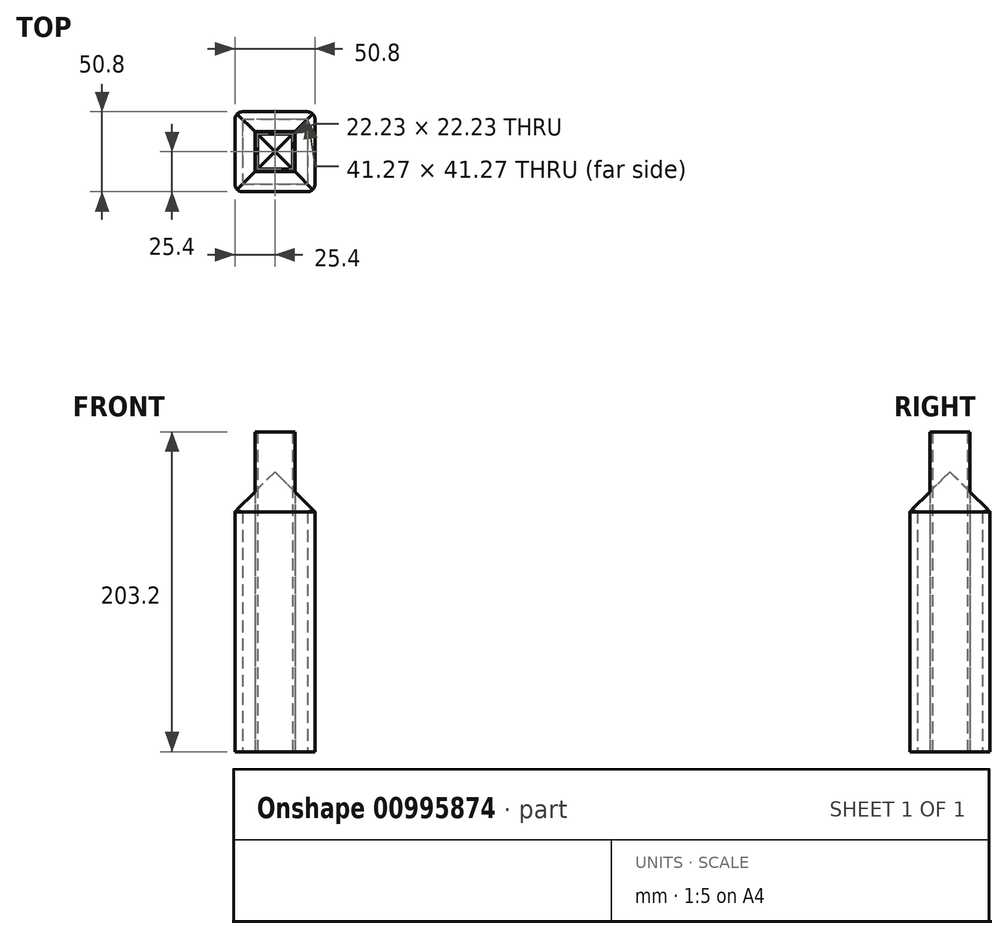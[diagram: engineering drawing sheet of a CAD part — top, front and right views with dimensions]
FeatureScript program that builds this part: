
annotation { "Feature Type Name" : "Feature", "Feature Type Description" : "" }
export const myFeature = defineFeature(function(context is Context, id is Id, definition is map)
    precondition{}
    {
        {
            var Q0;
            Q0=qCreatedBy(makeId("Top.planeOp"),FACE);
            var sketch = newSketch(context, id + "F0", { "sketchPlane" : qUnion([Q0])});
            skLineSegment(sketch, "E0.bottom", {"start": v(4.76, 0) * mm, "end": v(46.04, 0) * mm});
            skLineSegment(sketch, "E0.top", {"start": v(4.76, 50.8) * mm, "end": v(46.04, 50.8) * mm});
            skLineSegment(sketch, "E0.left", {"start": v(0, 4.76) * mm, "end": v(0, 46.04) * mm});
            skLineSegment(sketch, "E0.right", {"start": v(50.8, 4.76) * mm, "end": v(50.8, 46.04) * mm});
            skLineSegment(sketch, "E1.bottom", {"start": v(4.76, 46.04) * mm, "end": v(46.04, 46.04) * mm});
            skLineSegment(sketch, "E1.top", {"start": v(4.76, 4.76) * mm, "end": v(46.04, 4.76) * mm});
            skLineSegment(sketch, "E1.left", {"start": v(4.76, 46.04) * mm, "end": v(4.76, 4.76) * mm});
            skLineSegment(sketch, "E1.right", {"start": v(46.04, 46.04) * mm, "end": v(46.04, 4.76) * mm});
            skPoint(sketch, "E2.visualSharp", {"position": v(0, 50.8) * mm});
            skArc(sketch, "E2.filletArc", {"start": v(4.76, 50.8) * mm, "mid": v(1.4, 49.4) * mm, "end": v(0, 46.04) * mm});
            skPoint(sketch, "E3.visualSharp", {"position": v(50.8, 50.8) * mm});
            skArc(sketch, "E3.filletArc", {"start": v(50.8, 46.04) * mm, "mid": v(49.4, 49.4) * mm, "end": v(46.04, 50.8) * mm});
            skPoint(sketch, "E4.visualSharp", {"position": v(50.8, 0) * mm});
            skArc(sketch, "E4.filletArc", {"start": v(46.04, 0) * mm, "mid": v(49.4, 1.4) * mm, "end": v(50.8, 4.76) * mm});
            skPoint(sketch, "E5.visualSharp", {"position": v(0, 0) * mm});
            skArc(sketch, "E5.filletArc", {"start": v(0, 4.76) * mm, "mid": v(1.4, 1.4) * mm, "end": v(4.76, 0) * mm});
            skSolve(sketch);
        }
        {
            var Q0;
            Q0=makeQuery(id+"F0.imprint","IMPRINT",FACE,{"disambiguationData":[TD([[makeQuery(id+"F0.imprint","IMPRINT",EDGE,{"derivedFrom":sQuery(id+"F0.wireOp",EDGE,"E0.bottom")}),1.0]])]});
            extrude(context, id + "F1", {"entities" : qUnion([Q0]), "depth" : 152.4 * mm, "offsetDistance" : 25.4 * mm});
        }
        {
            var Q0;
            Q0=qCreatedBy(makeId("Top.planeOp"),FACE);
            var sketch = newSketch(context, id + "F2", { "sketchPlane" : qUnion([Q0])});
            skLineSegment(sketch, "E6.bottom", {"start": v(12.7, 38.1) * mm, "end": v(38.1, 38.1) * mm});
            skLineSegment(sketch, "E6.top", {"start": v(12.7, 12.7) * mm, "end": v(38.1, 12.7) * mm});
            skLineSegment(sketch, "E6.left", {"start": v(12.7, 38.1) * mm, "end": v(12.7, 12.7) * mm});
            skLineSegment(sketch, "E6.right", {"start": v(38.1, 38.1) * mm, "end": v(38.1, 12.7) * mm});
            skLineSegment(sketch, "E7.bottom", {"start": v(14.29, 36.51) * mm, "end": v(36.51, 36.51) * mm});
            skLineSegment(sketch, "E7.top", {"start": v(14.29, 14.29) * mm, "end": v(36.51, 14.29) * mm});
            skLineSegment(sketch, "E7.left", {"start": v(14.29, 36.51) * mm, "end": v(14.29, 14.29) * mm});
            skLineSegment(sketch, "E7.right", {"start": v(36.51, 36.51) * mm, "end": v(36.51, 14.29) * mm});
            skSolve(sketch);
        }
        {
            var Q0;
            Q0=makeQuery(id+"F1.opExtrude","CAP_FACE",FACE,{"disambiguationData":[OSD([sQuery(id+"F0.wireOp",EDGE,"E0.bottom"),sQuery(id+"F0.wireOp",EDGE,"E0.top"),sQuery(id+"F0.wireOp",EDGE,"E0.left"),sQuery(id+"F0.wireOp",EDGE,"E0.right"),sQuery(id+"F0.wireOp",EDGE,"E1.bottom"),sQuery(id+"F0.wireOp",EDGE,"E1.top"),sQuery(id+"F0.wireOp",EDGE,"E1.left"),sQuery(id+"F0.wireOp",EDGE,"E1.right"),sQuery(id+"F0.wireOp",EDGE,"E2.filletArc"),sQuery(id+"F0.wireOp",EDGE,"E3.filletArc"),sQuery(id+"F0.wireOp",EDGE,"E4.filletArc"),sQuery(id+"F0.wireOp",EDGE,"E5.filletArc")])],"isStart":false});
            var sketch = newSketch(context, id + "F3", { "sketchPlane" : qUnion([Q0])});
            skPoint(sketch, "E8.oppositeSnap0", {"position": v(50.8, 25.4) * mm});
            skLineSegment(sketch, "E8.bottom", {"start": v(0, 0) * mm, "end": v(50.8, 0) * mm});
            skLineSegment(sketch, "E8.top", {"start": v(0, 50.8) * mm, "end": v(50.8, 50.8) * mm});
            skLineSegment(sketch, "E8.left", {"start": v(0, 0) * mm, "end": v(0, 50.8) * mm});
            skLineSegment(sketch, "E8.right", {"start": v(50.8, 0) * mm, "end": v(50.8, 50.8) * mm});
            skSolve(sketch);
        }
        {
            var Q0;
            Q0=makeQuery(id+"F3.imprint","IMPRINT",FACE,{"disambiguationData":[TD([[makeQuery(id+"F3.imprint","IMPRINT",EDGE,{"derivedFrom":makeQuery(id+"F1.opExtrude","CAP_EDGE",EDGE,{"disambiguationData":[OSD([sQuery(id+"F0.wireOp",EDGE,"E1.bottom")])],"isStart":false})}),-1.0]])]});
            var Q1;
            Q1=makeQuery(id+"F3.imprint","IMPRINT",FACE,{"disambiguationData":[TD([[makeQuery(id+"F3.imprint","IMPRINT",EDGE,{"derivedFrom":makeQuery(id+"F1.opExtrude","CAP_EDGE",EDGE,{"disambiguationData":[OSD([sQuery(id+"F0.wireOp",EDGE,"E1.bottom")])],"isStart":false})}),1.0]])]});
            extrude(context, id + "F4", {"entities" : qUnion([Q0, Q1]), "depth" : 25.4 * mm, "offsetDistance" : 25.4 * mm});
        }
        {
            var Q0;
            Q0=makeQuery(id+"F4.opExtrude","CAP_EDGE",EDGE,{"disambiguationData":[OSD([sQuery(id+"F3.wireOp",EDGE,"E8.right")])],"isStart":false});
            var Q1;
            Q1=makeQuery(id+"F4.opExtrude","CAP_EDGE",EDGE,{"disambiguationData":[OSD([sQuery(id+"F3.wireOp",EDGE,"E8.top")])],"isStart":false});
            var Q2;
            Q2=makeQuery(id+"F4.opExtrude","CAP_EDGE",EDGE,{"disambiguationData":[OSD([sQuery(id+"F3.wireOp",EDGE,"E8.bottom")])],"isStart":false});
            var Q3;
            Q3=makeQuery(id+"F4.opExtrude","CAP_EDGE",EDGE,{"disambiguationData":[OSD([sQuery(id+"F3.wireOp",EDGE,"E8.left")])],"isStart":false});
            chamfer(context, id + "F5", {"entities" : qUnion([Q0, Q1, Q2, Q3]), "width" : 25.4 * mm});
        }
        {
            var Q0;
            Q0=makeQuery(id+"F2.imprint","IMPRINT",FACE,{"disambiguationData":[TD([[makeQuery(id+"F2.imprint","IMPRINT",EDGE,{"derivedFrom":sQuery(id+"F2.wireOp",EDGE,"E6.bottom")}),-1.0]])]});
            extrude(context, id + "F6", {"entities" : qUnion([Q0]), "depth" : 203.2 * mm, "offsetDistance" : 25.4 * mm});
        }
    });
